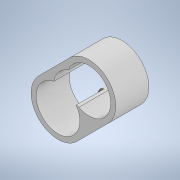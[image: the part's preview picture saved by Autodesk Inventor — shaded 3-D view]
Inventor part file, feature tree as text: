
AUTODESK INVENTOR PART (.ipt)
format: ipt  version: 2020 (Build 240168000, 168)  size: 207,872 bytes
history: native  units: in
note: dims shown in document units (in); Inventor stores cm internally (conversion verified against a paired STEP export)
features: extrude x4, sketch x4, fillet x2
ambient origin geometry x8: Origin, YZ Plane, XZ Plane, XY Plane, X Axis, Y Axis, Z Axis, Center Point
bodies: Solid1 (feature_tree)
feature tree (10):
  extrude  "Extrusion1"  Depth=0.9606in
  extrude  "Extrusion3"  TaperAngle=45.0deg  [1 undecoded]
  extrude  "Extrusion4"  Depth=0.4134in
  extrude  "Extrusion5"  Depth=0.1181in
  fillet  "Fillet1"  Radius=0.1181in
  fillet  "Fillet2"  Radius=0.1181in
  sketch  "Sketch1"  dims[d0=0.9724in d1=0.9606in]
  sketch  "Sketch3"  dims[d2=0.0in d3=45.0deg]
  sketch  "Sketch4"  dims[d4=0.0in d5=0.4134in]
  sketch  "Sketch5"  dims[d20=0.3346in d21=0.1181in d22=0.1181in d23=0.1181in d24=0.9606in d25=0.9606in d26=0.1772in d27=0.1181in d28=0.0in d32=0.9724in d33=0.9606in d34=0.0in d35=45.0deg d36=0.0in d37=0.4134in d38=0.3346in d39=0.1181in d40=0.1181in d41=0.1181in d42=0.9606in d43=0.9606in d44=0.1772in d45=0.6102in d46=0.0in d49=0.2165in d50=0.0787in d51=0.0394in d52=0.0in d53=0.0in d54=0.9724in d55=0.9606in d56=0.0in d57=45.0deg d58=0.0in d59=0.4134in d60=0.3346in d61=0.1181in d62=0.1181in d63=0.1181in d64=0.9606in d65=0.9606in d66=0.1772in d67=0.5906in d68=0.5906in d69=1.1811in d70=0.5906in d71=0.7283in d72=0.0in d73=0.1181in d74=0.1181in]
note: 1 required parameter value undecoded (feature->parameter linkage not recoverable at this tier; creation-order binding heuristic only, values carry confidence <= 0.55)
